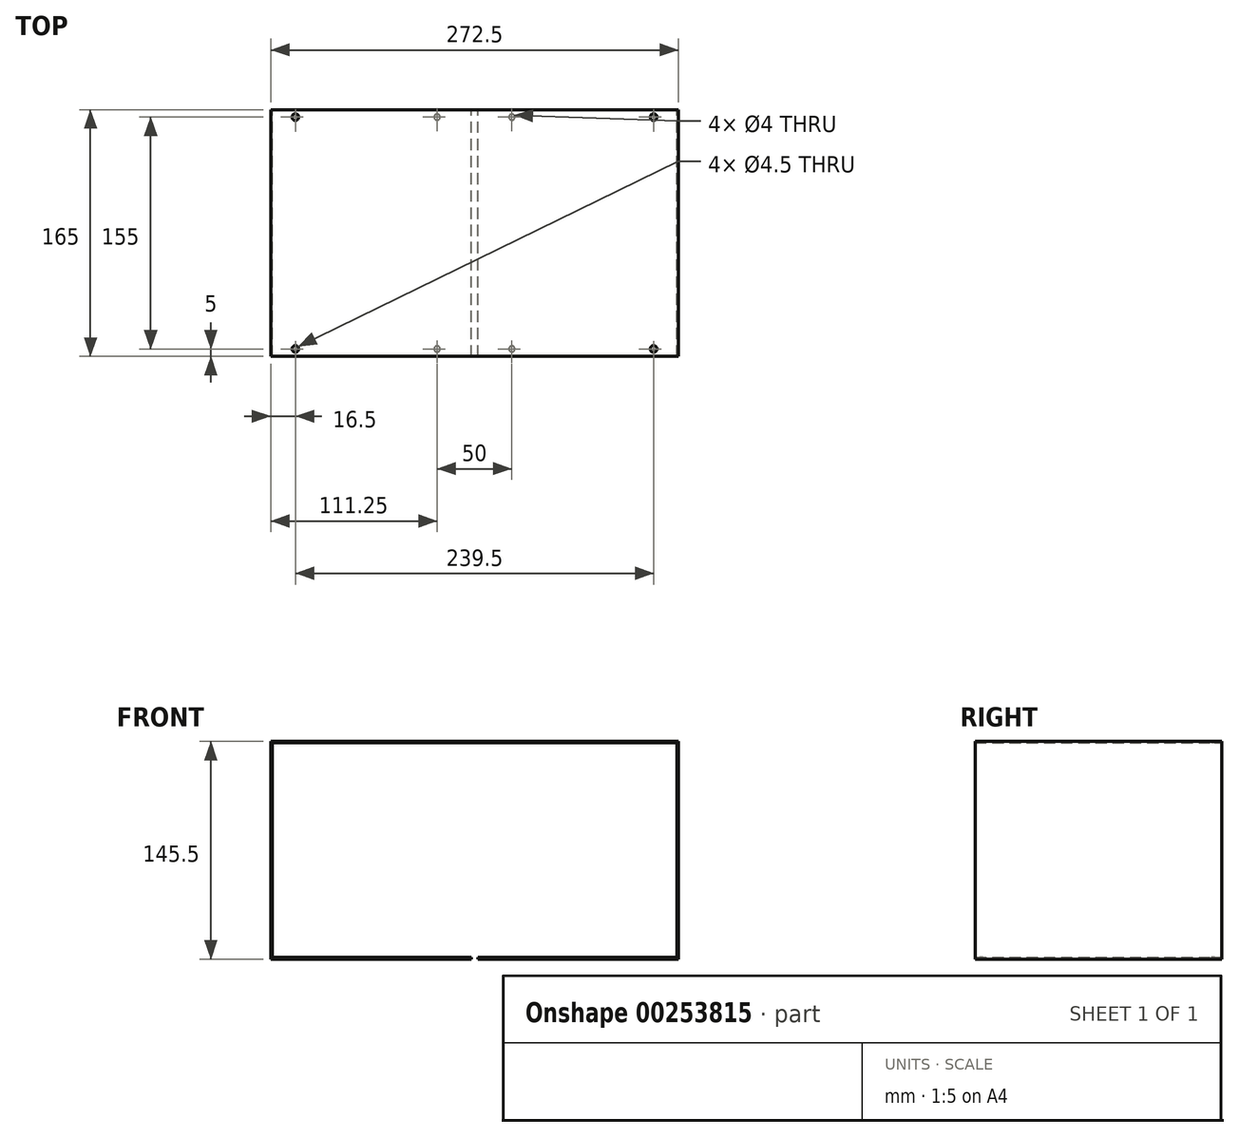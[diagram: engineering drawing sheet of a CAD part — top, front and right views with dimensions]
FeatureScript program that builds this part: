
annotation { "Feature Type Name" : "Feature", "Feature Type Description" : "" }
export const myFeature = defineFeature(function(context is Context, id is Id, definition is map)
    precondition{}
    {
        {
            var Q0;
            Q0=qCreatedBy(makeId("Front.planeOp"),FACE);
            var sketch = newSketch(context, id + "F0", { "sketchPlane" : qUnion([Q0])});
            skLineSegment(sketch, "E0", {"start": v(-136.25, 72.75) * mm, "end": v(136.25, 72.75) * mm});
            skLineSegment(sketch, "E1", {"start": v(136.25, 72.75) * mm, "end": v(136.25, -72.75) * mm});
            skLineSegment(sketch, "E2", {"start": v(136.25, -72.75) * mm, "end": v(2.25, -72.75) * mm});
            skLineSegment(sketch, "E3", {"start": v(2.25, -72.75) * mm, "end": v(2.25, -71.75) * mm});
            skLineSegment(sketch, "E4", {"start": v(2.25, -71.75) * mm, "end": v(135.25, -71.75) * mm});
            skLineSegment(sketch, "E5", {"start": v(135.25, -71.75) * mm, "end": v(135.25, 71.75) * mm});
            skLineSegment(sketch, "E6", {"start": v(135.25, 71.75) * mm, "end": v(-135.25, 71.75) * mm});
            skLineSegment(sketch, "E7", {"start": v(-135.25, 71.75) * mm, "end": v(-135.25, -71.75) * mm});
            skLineSegment(sketch, "E8", {"start": v(-135.25, -71.75) * mm, "end": v(-2.25, -71.75) * mm});
            skLineSegment(sketch, "E9", {"start": v(-2.25, -71.75) * mm, "end": v(-2.25, -72.75) * mm});
            skLineSegment(sketch, "E10", {"start": v(-2.25, -72.75) * mm, "end": v(-136.25, -72.75) * mm});
            skLineSegment(sketch, "E11", {"start": v(-136.25, -72.75) * mm, "end": v(-136.25, 72.75) * mm});
            skSolve(sketch);
        }
        {
            var Q0;
            Q0 = qSketchRegion(id + "F0", true);
            extrude(context, id + "F1", {"entities" : qUnion([Q0]), "depth" : 165 * mm});
        }
        {
            var Q0;
            Q0=makeQuery(id+"F1.opExtrude","SWEPT_FACE",FACE,{"disambiguationData":[OSD([sQuery(id+"F0.wireOp",EDGE,"E2")])]});
            var sketch = newSketch(context, id + "F2", { "sketchPlane" : qUnion([Q0])});
            skCircle(sketch, "E12", {"center": v(25, 160) * mm, "radius": 2 * mm});
            skCircle(sketch, "E13", {"center": v(-25, 160) * mm, "radius": 2 * mm});
            skCircle(sketch, "E14", {"center": v(25, 5) * mm, "radius": 2 * mm});
            skCircle(sketch, "E15", {"center": v(-25, 5) * mm, "radius": 2 * mm});
            skSolve(sketch);
        }
        {
            var Q0;
            Q0 = qSketchRegion(id + "F2", true);
            extrude(context, id + "F3", {"entities" : qUnion([Q0]), "operationType" : NewBodyOperationType.REMOVE, "endBound" : BoundingType.UP_TO_NEXT, "oppositeDirection" : true, "depth" : 25 * mm});
        }
        {
            var Q0;
            Q0=makeQuery(id+"F1.opExtrude","SWEPT_FACE",FACE,{"disambiguationData":[OSD([sQuery(id+"F0.wireOp",EDGE,"E0")])]});
            var sketch = newSketch(context, id + "F4", { "sketchPlane" : qUnion([Q0])});
            skCircle(sketch, "E16", {"center": v(-119.75, -5) * mm, "radius": 2.25 * mm});
            skCircle(sketch, "E17", {"center": v(119.75, -5) * mm, "radius": 2.25 * mm});
            skCircle(sketch, "E18", {"center": v(-119.75, -160) * mm, "radius": 2.25 * mm});
            skCircle(sketch, "E19", {"center": v(119.75, -160) * mm, "radius": 2.25 * mm});
            skSolve(sketch);
        }
        {
            var Q0;
            Q0 = qSketchRegion(id + "F4", true);
            extrude(context, id + "F5", {"entities" : qUnion([Q0]), "operationType" : NewBodyOperationType.REMOVE, "endBound" : BoundingType.UP_TO_NEXT, "oppositeDirection" : true, "depth" : 25 * mm});
        }
    });
